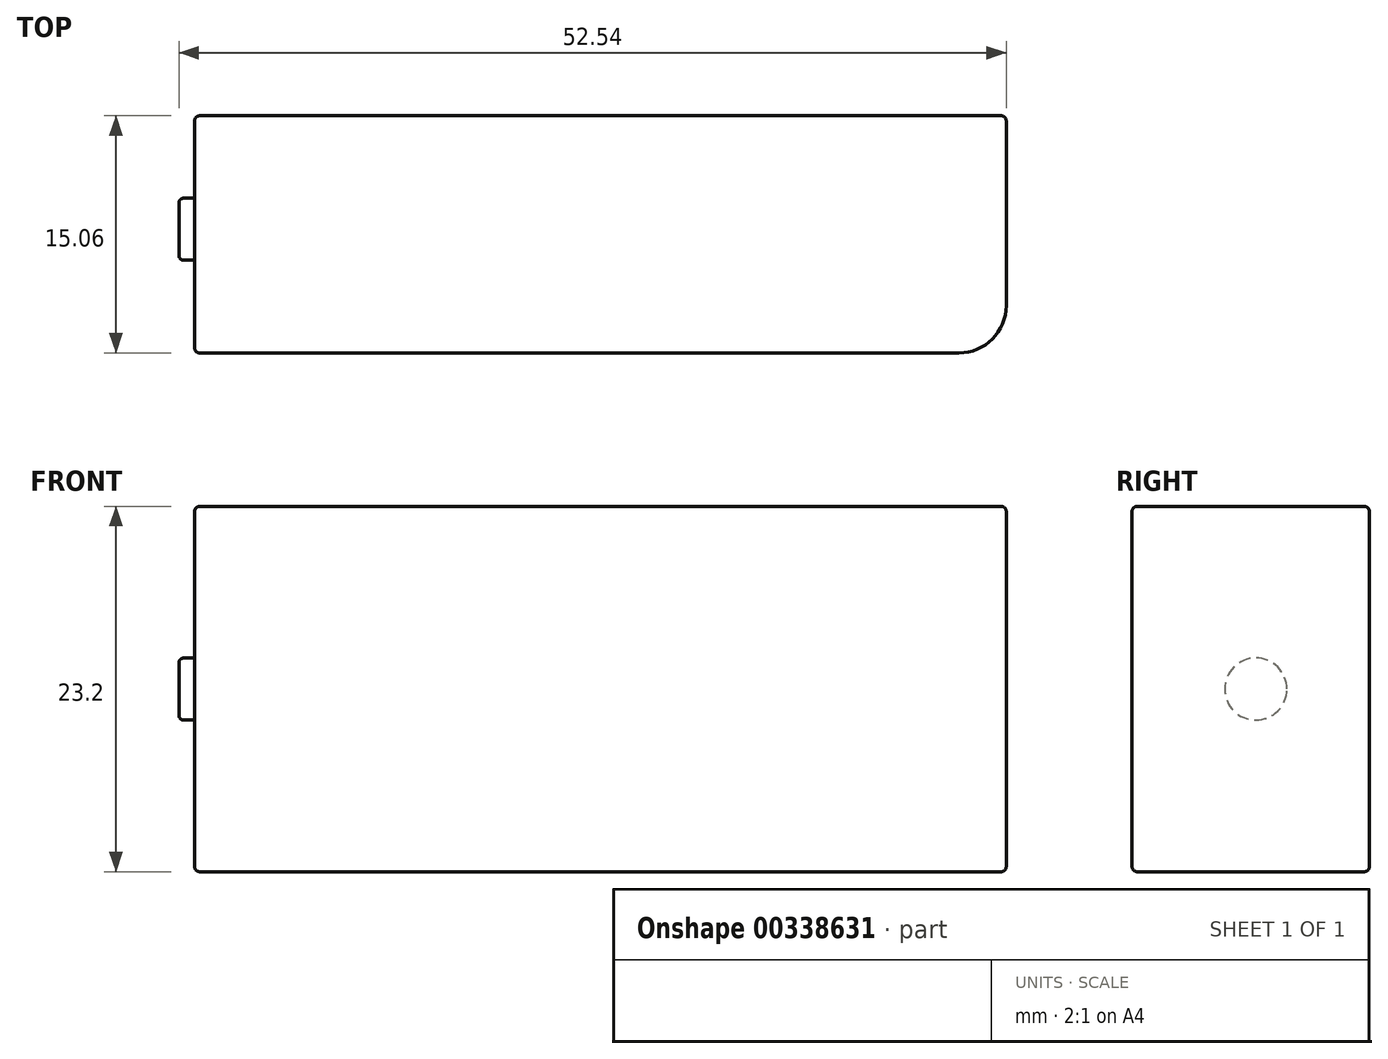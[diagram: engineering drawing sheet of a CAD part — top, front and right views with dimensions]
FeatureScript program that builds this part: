
annotation { "Feature Type Name" : "Feature", "Feature Type Description" : "" }
export const myFeature = defineFeature(function(context is Context, id is Id, definition is map)
    precondition{}
    {
        {
            var Q0;
            Q0=qCreatedBy(makeId("Front.planeOp"),FACE);
            var sketch = newSketch(context, id + "F0", { "sketchPlane" : qUnion([Q0])});
            skLineSegment(sketch, "E0.bottom", {"start": v(-25.77, 11.6) * mm, "end": v(25.77, 11.6) * mm});
            skLineSegment(sketch, "E0.top", {"start": v(-25.77, -11.6) * mm, "end": v(25.77, -11.6) * mm});
            skLineSegment(sketch, "E0.left", {"start": v(-25.77, 11.6) * mm, "end": v(-25.77, -11.6) * mm});
            skLineSegment(sketch, "E0.right", {"start": v(25.77, 11.6) * mm, "end": v(25.77, -11.6) * mm});
            skPoint(sketch, "E0.middle", {"position": v(0, 0) * mm});
            skSolve(sketch);
        }
        {
            var Q0;
            Q0 = qSketchRegion(id + "F0", true);
            extrude(context, id + "F1", {"entities" : qUnion([Q0]), "depth" : 15.06 * mm, "offsetDistance" : 25 * mm});
        }
        {
            var Q0;
            Q0=makeQuery(id+"F1.opExtrude","SWEPT_FACE",FACE,{"disambiguationData":[OSD([sQuery(id+"F0.wireOp",EDGE,"E0.left")])]});
            var sketch = newSketch(context, id + "F2", { "sketchPlane" : qUnion([Q0])});
            skCircle(sketch, "E1", {"center": v(7.2, 0) * mm, "radius": 1.97 * mm});
            skPoint(sketch, "E1.centerSnap0", {"position": v(15.06, 0) * mm});
            skSolve(sketch);
        }
        {
            var Q0;
            Q0 = qSketchRegion(id + "F2", true);
            extrude(context, id + "F3", {"entities" : qUnion([Q0]), "operationType" : NewBodyOperationType.ADD, "depth" : 1 * mm, "offsetDistance" : 25 * mm});
        }
        {
            var Q0;
            Q0=makeQuery(id+"F3.opExtrude","CAP_EDGE",EDGE,{"disambiguationData":[OSD([sQuery(id+"F2.wireOp",EDGE,"E1")])],"isStart":false});
            fillet(context, id + "F4", {"entities" : qUnion([Q0]), "radius" : 0.3 * mm, "tangentPropagation" : true, "allowEdgeOverflow" : false});
        }
        {
            var Q0;
            Q0=makeQuery(id+"F1.opExtrude","CAP_EDGE",EDGE,{"disambiguationData":[OSD([sQuery(id+"F0.wireOp",EDGE,"E0.right")])],"isStart":false});
            fillet(context, id + "F5", {"entities" : qUnion([Q0]), "radius" : 3 * mm, "tangentPropagation" : true, "allowEdgeOverflow" : false});
        }
        {
            var Q0;
            Q0=makeQuery(id+"F1.opExtrude","CAP_EDGE",EDGE,{"disambiguationData":[OSD([sQuery(id+"F0.wireOp",EDGE,"E0.top")])],"isStart":false});
            var Q1;
            Q1=makeQuery(id+"F1.opExtrude","CAP_EDGE",EDGE,{"disambiguationData":[OSD([sQuery(id+"F0.wireOp",EDGE,"E0.bottom")])],"isStart":false});
            var Q2;
            Q2=makeQuery(id+"F1.opExtrude","CAP_EDGE",EDGE,{"disambiguationData":[OSD([sQuery(id+"F0.wireOp",EDGE,"E0.left")])],"isStart":false});
            var Q3;
            Q3=makeQuery(id+"F1.opExtrude","SWEPT_EDGE",EDGE,{"disambiguationData":[OSD([sQuery(id+"F0.wireOp",EDGE,"E0.top"),sQuery(id+"F0.wireOp",EDGE,"E0.left")])]});
            var Q4;
            Q4=makeQuery(id+"F1.opExtrude","CAP_EDGE",EDGE,{"disambiguationData":[OSD([sQuery(id+"F0.wireOp",EDGE,"E0.left")])],"isStart":true});
            var Q5;
            Q5=makeQuery(id+"F1.opExtrude","SWEPT_EDGE",EDGE,{"disambiguationData":[OSD([sQuery(id+"F0.wireOp",EDGE,"E0.bottom"),sQuery(id+"F0.wireOp",EDGE,"E0.left")])]});
            var Q6;
            Q6=makeQuery(id+"F1.opExtrude","CAP_EDGE",EDGE,{"disambiguationData":[OSD([sQuery(id+"F0.wireOp",EDGE,"E0.top")])],"isStart":true});
            var Q7;
            Q7=makeQuery(id+"F1.opExtrude","CAP_EDGE",EDGE,{"disambiguationData":[OSD([sQuery(id+"F0.wireOp",EDGE,"E0.bottom")])],"isStart":true});
            var Q8;
            Q8=makeQuery(id+"F1.opExtrude","CAP_EDGE",EDGE,{"disambiguationData":[OSD([sQuery(id+"F0.wireOp",EDGE,"E0.right")])],"isStart":true});
            fillet(context, id + "F6", {"entities" : qUnion([Q0, Q1, Q2, Q3, Q4, Q5, Q6, Q7, Q8]), "radius" : 0.3 * mm, "tangentPropagation" : true, "allowEdgeOverflow" : false});
        }
    });
